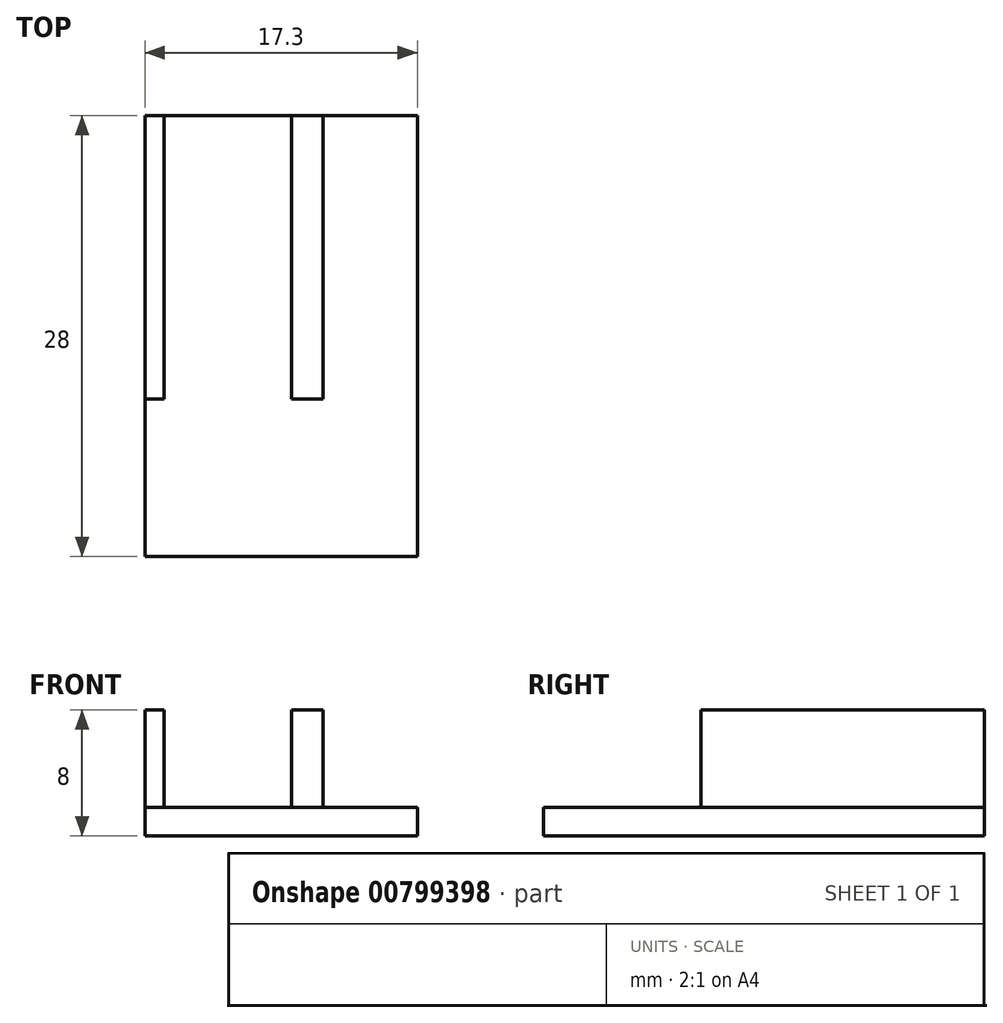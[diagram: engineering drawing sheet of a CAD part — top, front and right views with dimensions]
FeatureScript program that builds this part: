
annotation { "Feature Type Name" : "Feature", "Feature Type Description" : "" }
export const myFeature = defineFeature(function(context is Context, id is Id, definition is map)
    precondition{}
    {
        {
            var Q0;
            Q0=qCreatedBy(makeId("Top.planeOp"),FACE);
            var sketch = newSketch(context, id + "F0", { "sketchPlane" : qUnion([Q0])});
            skLineSegment(sketch, "E0.bottom", {"start": v(4.05, -9) * mm, "end": v(-4.05, -9) * mm});
            skLineSegment(sketch, "E0.top", {"start": v(4.05, 9) * mm, "end": v(-4.05, 9) * mm});
            skLineSegment(sketch, "E0.left", {"start": v(4.05, -9) * mm, "end": v(4.05, 9) * mm});
            skLineSegment(sketch, "E0.right", {"start": v(-4.05, -9) * mm, "end": v(-4.05, 9) * mm});
            skPoint(sketch, "E0.middle", {"position": v(0, 0) * mm});
            skLineSegment(sketch, "E1.bottom", {"start": v(-4.05, 9) * mm, "end": v(-5.25, 9) * mm});
            skLineSegment(sketch, "E1.top", {"start": v(-4.05, -9) * mm, "end": v(-5.25, -9) * mm});
            skLineSegment(sketch, "E1.left", {"start": v(-4.05, 9) * mm, "end": v(-4.05, -9) * mm});
            skLineSegment(sketch, "E1.right", {"start": v(-5.25, 9) * mm, "end": v(-5.25, -9) * mm});
            skLineSegment(sketch, "E2.bottom", {"start": v(4.05, 9) * mm, "end": v(6.05, 9) * mm});
            skLineSegment(sketch, "E2.top", {"start": v(4.05, -9) * mm, "end": v(6.05, -9) * mm});
            skLineSegment(sketch, "E2.left", {"start": v(4.05, 9) * mm, "end": v(4.05, -9) * mm});
            skLineSegment(sketch, "E2.right", {"start": v(6.05, 9) * mm, "end": v(6.05, -9) * mm});
            skLineSegment(sketch, "E3.bottom", {"start": v(-5.25, -9) * mm, "end": v(6.05, -9) * mm});
            skLineSegment(sketch, "E3.top", {"start": v(-5.25, -19) * mm, "end": v(6.05, -19) * mm});
            skLineSegment(sketch, "E3.left", {"start": v(-5.25, -9) * mm, "end": v(-5.25, -19) * mm});
            skLineSegment(sketch, "E3.right", {"start": v(6.05, -9) * mm, "end": v(6.05, -19) * mm});
            skLineSegment(sketch, "E4.left", {"start": v(-5.25, 9) * mm, "end": v(-5.25, -19) * mm});
            skLineSegment(sketch, "E5.bottom", {"start": v(6.05, 9) * mm, "end": v(12.05, 9) * mm});
            skLineSegment(sketch, "E5.top", {"start": v(6.05, -19) * mm, "end": v(12.05, -19) * mm});
            skLineSegment(sketch, "E5.left", {"start": v(6.05, 9) * mm, "end": v(6.05, -19) * mm});
            skLineSegment(sketch, "E5.right", {"start": v(12.05, 9) * mm, "end": v(12.05, -19) * mm});
            skSolve(sketch);
        }
        {
            var Q0;
            Q0=makeQuery(id+"F0.imprint","IMPRINT",FACE,{"disambiguationData":[TD([[makeQuery(id+"F0.imprint","IMPRINT",EDGE,{"derivedFrom":sQuery(id+"F0.wireOp",EDGE,"E3.top")}),1.0]])]});
            var Q1;
            Q1=makeQuery(id+"F0.imprint","IMPRINT",FACE,{"disambiguationData":[TD([[makeQuery(id+"F0.imprint","IMPRINT",EDGE,{"derivedFrom":sQuery(id+"F0.wireOp",EDGE,"E0.top")}),1.0]])]});
            var Q2;
            {var subQ3=sQuery(id+"F0.wireOp",EDGE,"E4.bottom");Q2=makeQuery(id+"F0.imprint","IMPRINT",FACE,{"disambiguationData":[TD([[makeQuery(id+"F0.imprint","IMPRINT",EDGE,{"derivedFrom":subQ3}),1.0]])]});}
            var Q3;
            {var subQ3=sQuery(id+"F0.wireOp",EDGE,"E5.bottom");Q3=makeQuery(id+"F0.imprint","IMPRINT",FACE,{"disambiguationData":[TD([[makeQuery(id+"F0.imprint","IMPRINT",EDGE,{"derivedFrom":subQ3}),-1.0]])]});}
            extrude(context, id + "F1", {"entities" : qUnion([Q0, Q1, Q2, Q3]), "depth" : 1.8 * mm, "offsetDistance" : 25 * mm});
        }
        {
            var Q0;
            Q0=makeQuery(id+"F0.imprint","IMPRINT",FACE,{"disambiguationData":[TD([[makeQuery(id+"F0.imprint","IMPRINT",EDGE,{"derivedFrom":sQuery(id+"F0.wireOp",EDGE,"E1.bottom")}),1.0]])]});
            var Q1;
            Q1=makeQuery(id+"F0.imprint","IMPRINT",FACE,{"disambiguationData":[TD([[makeQuery(id+"F0.imprint","IMPRINT",EDGE,{"derivedFrom":sQuery(id+"F0.wireOp",EDGE,"E2.bottom")}),-1.0]])]});
            extrude(context, id + "F2", {"entities" : qUnion([Q0, Q1]), "operationType" : NewBodyOperationType.ADD, "depth" : 8 * mm, "offsetDistance" : 25 * mm});
        }
    });
